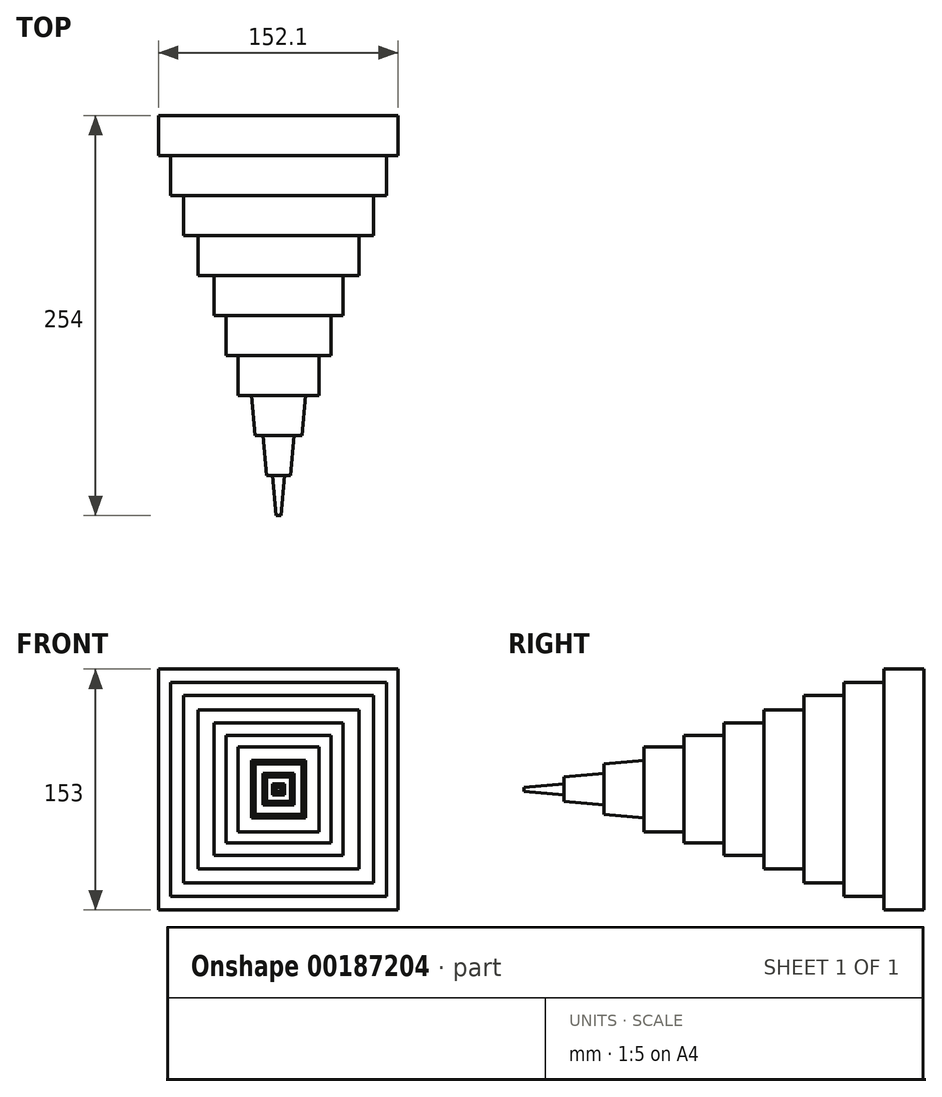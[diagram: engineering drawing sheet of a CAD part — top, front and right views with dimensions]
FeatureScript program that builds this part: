
annotation { "Feature Type Name" : "Feature", "Feature Type Description" : "" }
export const myFeature = defineFeature(function(context is Context, id is Id, definition is map)
    precondition{}
    {
        {
            var Q0;
            Q0=qCreatedBy(makeId("Front.planeOp"),FACE);
            var sketch = newSketch(context, id + "F0", { "sketchPlane" : qUnion([Q0])});
            skLineSegment(sketch, "E0.bottom", {"start": v(-76.2, 76.35) * mm, "end": v(75.9, 76.35) * mm});
            skLineSegment(sketch, "E0.top", {"start": v(-76.2, -76.65) * mm, "end": v(75.9, -76.65) * mm});
            skLineSegment(sketch, "E0.left", {"start": v(-76.2, 76.35) * mm, "end": v(-76.2, -76.65) * mm});
            skLineSegment(sketch, "E0.right", {"start": v(75.9, 76.35) * mm, "end": v(75.9, -76.65) * mm});
            skSolve(sketch);
        }
        {
            var Q0;
            Q0 = qSketchRegion(id + "F0", true);
            extrude(context, id + "F1", {"entities" : qUnion([Q0]), "depth" : 25.4 * mm});
        }
        {
            var Q0;
            Q0=makeQuery(id+"F1.opExtrude","CAP_FACE",FACE,{"disambiguationData":[OSD([sQuery(id+"F0.wireOp",EDGE,"E0.bottom"),sQuery(id+"F0.wireOp",EDGE,"E0.top"),sQuery(id+"F0.wireOp",EDGE,"E0.left"),sQuery(id+"F0.wireOp",EDGE,"E0.right")])],"isStart":false});
            var sketch = newSketch(context, id + "F2", { "sketchPlane" : qUnion([Q0])});
            skLineSegment(sketch, "E1.bottom", {"start": v(68.67, -67.92) * mm, "end": v(-68.67, -67.92) * mm});
            skLineSegment(sketch, "E1.top", {"start": v(68.67, 67.92) * mm, "end": v(-68.67, 67.92) * mm});
            skLineSegment(sketch, "E1.left", {"start": v(68.67, -67.92) * mm, "end": v(68.67, 67.92) * mm});
            skLineSegment(sketch, "E1.right", {"start": v(-68.67, -67.92) * mm, "end": v(-68.67, 67.92) * mm});
            skPoint(sketch, "E1.middle", {"position": v(0, 0) * mm});
            skSolve(sketch);
        }
        {
            var Q0;
            Q0 = qSketchRegion(id + "F2", true);
            extrude(context, id + "F3", {"entities" : qUnion([Q0]), "operationType" : NewBodyOperationType.ADD, "depth" : 25.4 * mm});
        }
        {
            var Q0;
            Q0=makeQuery(id+"F3.opExtrude","CAP_FACE",FACE,{"disambiguationData":[OSD([sQuery(id+"F2.wireOp",EDGE,"E1.bottom"),sQuery(id+"F2.wireOp",EDGE,"E1.top"),sQuery(id+"F2.wireOp",EDGE,"E1.left"),sQuery(id+"F2.wireOp",EDGE,"E1.right")])],"isStart":false});
            var sketch = newSketch(context, id + "F4", { "sketchPlane" : qUnion([Q0])});
            skLineSegment(sketch, "E2.bottom", {"start": v(60.24, -59.48) * mm, "end": v(-60.24, -59.48) * mm});
            skLineSegment(sketch, "E2.top", {"start": v(60.24, 59.48) * mm, "end": v(-60.24, 59.48) * mm});
            skLineSegment(sketch, "E2.left", {"start": v(60.24, -59.48) * mm, "end": v(60.24, 59.48) * mm});
            skLineSegment(sketch, "E2.right", {"start": v(-60.24, -59.48) * mm, "end": v(-60.24, 59.48) * mm});
            skPoint(sketch, "E2.middle", {"position": v(0, 0) * mm});
            skSolve(sketch);
        }
        {
            var Q0;
            Q0 = qSketchRegion(id + "F4", true);
            extrude(context, id + "F5", {"entities" : qUnion([Q0]), "operationType" : NewBodyOperationType.ADD, "depth" : 25.4 * mm});
        }
        {
            var Q0;
            Q0=makeQuery(id+"F5.opExtrude","CAP_FACE",FACE,{"disambiguationData":[OSD([sQuery(id+"F4.wireOp",EDGE,"E2.bottom"),sQuery(id+"F4.wireOp",EDGE,"E2.top"),sQuery(id+"F4.wireOp",EDGE,"E2.left"),sQuery(id+"F4.wireOp",EDGE,"E2.right")])],"isStart":false});
            var sketch = newSketch(context, id + "F6", { "sketchPlane" : qUnion([Q0])});
            skLineSegment(sketch, "E3.bottom", {"start": v(51.2, -50.45) * mm, "end": v(-51.2, -50.45) * mm});
            skLineSegment(sketch, "E3.top", {"start": v(51.2, 50.45) * mm, "end": v(-51.2, 50.45) * mm});
            skLineSegment(sketch, "E3.left", {"start": v(51.2, -50.45) * mm, "end": v(51.2, 50.45) * mm});
            skLineSegment(sketch, "E3.right", {"start": v(-51.2, -50.45) * mm, "end": v(-51.2, 50.45) * mm});
            skPoint(sketch, "E3.middle", {"position": v(0, 0) * mm});
            skSolve(sketch);
        }
        {
            var Q0;
            Q0 = qSketchRegion(id + "F6", true);
            extrude(context, id + "F7", {"entities" : qUnion([Q0]), "operationType" : NewBodyOperationType.ADD, "depth" : 25.4 * mm});
        }
        {
            var Q0;
            Q0=makeQuery(id+"F7.opExtrude","CAP_FACE",FACE,{"disambiguationData":[OSD([sQuery(id+"F6.wireOp",EDGE,"E3.bottom"),sQuery(id+"F6.wireOp",EDGE,"E3.top"),sQuery(id+"F6.wireOp",EDGE,"E3.left"),sQuery(id+"F6.wireOp",EDGE,"E3.right")])],"isStart":false});
            var sketch = newSketch(context, id + "F8", { "sketchPlane" : qUnion([Q0])});
            skLineSegment(sketch, "E4.bottom", {"start": v(40.96, -42.02) * mm, "end": v(-40.96, -42.02) * mm});
            skLineSegment(sketch, "E4.top", {"start": v(40.96, 42.02) * mm, "end": v(-40.96, 42.02) * mm});
            skLineSegment(sketch, "E4.left", {"start": v(40.96, -42.02) * mm, "end": v(40.96, 42.02) * mm});
            skLineSegment(sketch, "E4.right", {"start": v(-40.96, -42.02) * mm, "end": v(-40.96, 42.02) * mm});
            skPoint(sketch, "E4.middle", {"position": v(0, 0) * mm});
            skSolve(sketch);
        }
        {
            var Q0;
            Q0 = qSketchRegion(id + "F8", true);
            extrude(context, id + "F9", {"entities" : qUnion([Q0]), "operationType" : NewBodyOperationType.ADD, "depth" : 25.4 * mm});
        }
        {
            var Q0;
            Q0=makeQuery(id+"F9.opExtrude","CAP_FACE",FACE,{"disambiguationData":[OSD([sQuery(id+"F8.wireOp",EDGE,"E4.bottom"),sQuery(id+"F8.wireOp",EDGE,"E4.top"),sQuery(id+"F8.wireOp",EDGE,"E4.left"),sQuery(id+"F8.wireOp",EDGE,"E4.right")])],"isStart":false});
            var sketch = newSketch(context, id + "F10", { "sketchPlane" : qUnion([Q0])});
            skLineSegment(sketch, "E5.bottom", {"start": v(33.43, -34.18) * mm, "end": v(-33.43, -34.18) * mm});
            skLineSegment(sketch, "E5.top", {"start": v(33.43, 34.18) * mm, "end": v(-33.43, 34.18) * mm});
            skLineSegment(sketch, "E5.left", {"start": v(33.43, -34.18) * mm, "end": v(33.43, 34.18) * mm});
            skLineSegment(sketch, "E5.right", {"start": v(-33.43, -34.18) * mm, "end": v(-33.43, 34.18) * mm});
            skPoint(sketch, "E5.middle", {"position": v(0, 0) * mm});
            skSolve(sketch);
        }
        {
            var Q0;
            Q0 = qSketchRegion(id + "F10", true);
            extrude(context, id + "F11", {"entities" : qUnion([Q0]), "operationType" : NewBodyOperationType.ADD, "depth" : 25.4 * mm});
        }
        {
            var Q0;
            Q0=makeQuery(id+"F11.opExtrude","CAP_FACE",FACE,{"disambiguationData":[OSD([sQuery(id+"F10.wireOp",EDGE,"E5.bottom"),sQuery(id+"F10.wireOp",EDGE,"E5.top"),sQuery(id+"F10.wireOp",EDGE,"E5.left"),sQuery(id+"F10.wireOp",EDGE,"E5.right")])],"isStart":false});
            var sketch = newSketch(context, id + "F12", { "sketchPlane" : qUnion([Q0])});
            skLineSegment(sketch, "E6.bottom", {"start": v(25.6, -26.96) * mm, "end": v(-25.6, -26.96) * mm});
            skLineSegment(sketch, "E6.top", {"start": v(25.6, 26.96) * mm, "end": v(-25.6, 26.96) * mm});
            skLineSegment(sketch, "E6.left", {"start": v(25.6, -26.96) * mm, "end": v(25.6, 26.96) * mm});
            skLineSegment(sketch, "E6.right", {"start": v(-25.6, -26.96) * mm, "end": v(-25.6, 26.96) * mm});
            skPoint(sketch, "E6.middle", {"position": v(0, 0) * mm});
            skSolve(sketch);
        }
        {
            var Q0;
            Q0 = qSketchRegion(id + "F12", true);
            extrude(context, id + "F13", {"entities" : qUnion([Q0]), "operationType" : NewBodyOperationType.ADD, "depth" : 25.4 * mm});
        }
        {
            var Q0;
            Q0=makeQuery(id+"F13.opExtrude","CAP_FACE",FACE,{"disambiguationData":[OSD([sQuery(id+"F12.wireOp",EDGE,"E6.bottom"),sQuery(id+"F12.wireOp",EDGE,"E6.top"),sQuery(id+"F12.wireOp",EDGE,"E6.left"),sQuery(id+"F12.wireOp",EDGE,"E6.right")])],"isStart":false});
            var sketch = newSketch(context, id + "F14", { "sketchPlane" : qUnion([Q0])});
            skLineSegment(sketch, "E7.bottom", {"start": v(17.17, -18.22) * mm, "end": v(-17.17, -18.22) * mm});
            skLineSegment(sketch, "E7.top", {"start": v(17.17, 18.22) * mm, "end": v(-17.17, 18.22) * mm});
            skLineSegment(sketch, "E7.left", {"start": v(17.17, -18.22) * mm, "end": v(17.17, 18.22) * mm});
            skLineSegment(sketch, "E7.right", {"start": v(-17.17, -18.22) * mm, "end": v(-17.17, 18.22) * mm});
            skPoint(sketch, "E7.middle", {"position": v(0, 0) * mm});
            skSolve(sketch);
        }
        {
            var Q0;
            Q0 = qSketchRegion(id + "F14", true);
            extrude(context, id + "F15", {"entities" : qUnion([Q0]), "operationType" : NewBodyOperationType.ADD, "depth" : 25.4 * mm, "hasDraft" : true, "draftAngle" : 5 * degree, "draftPullDirection" : true});
        }
        {
            var Q0;
            Q0=makeQuery(id+"F15.opExtrude","CAP_FACE",FACE,{"disambiguationData":[OSD([sQuery(id+"F14.wireOp",EDGE,"E7.bottom"),sQuery(id+"F14.wireOp",EDGE,"E7.top"),sQuery(id+"F14.wireOp",EDGE,"E7.left"),sQuery(id+"F14.wireOp",EDGE,"E7.right")])],"isStart":false});
            var sketch = newSketch(context, id + "F16", { "sketchPlane" : qUnion([Q0])});
            skLineSegment(sketch, "E8.bottom", {"start": v(9.94, -10.09) * mm, "end": v(-9.94, -10.09) * mm});
            skLineSegment(sketch, "E8.top", {"start": v(9.94, 10.09) * mm, "end": v(-9.94, 10.09) * mm});
            skLineSegment(sketch, "E8.left", {"start": v(9.94, -10.09) * mm, "end": v(9.94, 10.09) * mm});
            skLineSegment(sketch, "E8.right", {"start": v(-9.94, -10.09) * mm, "end": v(-9.94, 10.09) * mm});
            skPoint(sketch, "E8.middle", {"position": v(0, 0) * mm});
            skSolve(sketch);
        }
        {
            var Q0;
            Q0 = qSketchRegion(id + "F16", true);
            extrude(context, id + "F17", {"entities" : qUnion([Q0]), "operationType" : NewBodyOperationType.ADD, "depth" : 25.4 * mm, "hasDraft" : true, "draftAngle" : 5 * degree, "draftPullDirection" : true});
        }
        {
            var Q0;
            Q0=makeQuery(id+"F17.opExtrude","CAP_FACE",FACE,{"disambiguationData":[OSD([sQuery(id+"F16.wireOp",EDGE,"E8.bottom"),sQuery(id+"F16.wireOp",EDGE,"E8.top"),sQuery(id+"F16.wireOp",EDGE,"E8.left"),sQuery(id+"F16.wireOp",EDGE,"E8.right")])],"isStart":false});
            var sketch = newSketch(context, id + "F18", { "sketchPlane" : qUnion([Q0])});
            skLineSegment(sketch, "E9.bottom", {"start": v(3.92, -3.46) * mm, "end": v(-3.92, -3.46) * mm});
            skLineSegment(sketch, "E9.top", {"start": v(3.92, 3.46) * mm, "end": v(-3.92, 3.46) * mm});
            skLineSegment(sketch, "E9.left", {"start": v(3.92, -3.46) * mm, "end": v(3.92, 3.46) * mm});
            skLineSegment(sketch, "E9.right", {"start": v(-3.92, -3.46) * mm, "end": v(-3.92, 3.46) * mm});
            skPoint(sketch, "E9.middle", {"position": v(0, 0) * mm});
            skSolve(sketch);
        }
        {
            var Q0;
            Q0 = qSketchRegion(id + "F18", true);
            extrude(context, id + "F19", {"entities" : qUnion([Q0]), "operationType" : NewBodyOperationType.ADD, "depth" : 25.4 * mm, "hasDraft" : true, "draftAngle" : 5 * degree, "draftPullDirection" : true});
        }
    });
